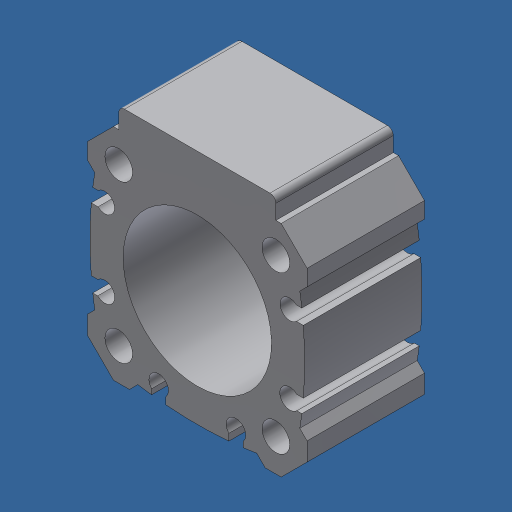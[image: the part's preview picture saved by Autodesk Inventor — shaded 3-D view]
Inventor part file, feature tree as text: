
AUTODESK INVENTOR PART (.ipt)
format: ipt  version: 2024.3 (Build 283343000, 343)  size: 252,928 bytes
history: native  units: mm (DEFAULTED — no unit token found)
features: other x1, extrude x1, sketch x1
ambient origin geometry x8: Origin, YZ Plane, XZ Plane, XY Plane, X Axis, Y Axis, Z Axis, Center Point
bodies: Body1 (feature_tree)
feature tree (3):
  other  "Finish - None"
  extrude  "PHD, 32MM"  Depth=54.69358mm
  sketch  "Sketch1"  dims[d0=54.69358mm d2=54.69358mm d3=155.869159mm d4=155.869159mm d6=32.106mm d7=27.991mm d8=2.54mm d10=15.7355mm d11=26.721mm d12=18.146886mm d13=23.52mm d14=135.0deg d15=17.916886mm d16=3.488886mm d17=135.0deg d18=22.174mm d19=9.8935mm d22=22.610478mm d23=20.015mm d24=8.357mm d25=4.242mm d26=6.8205mm d27=8.357mm d28=4.335353mm d29=6.8205mm d30=9.8935mm d31=77.93458mm d32=22.174mm d33=12.852mm d34=45.0deg d35=14.428mm d37=18.405886mm d38=135.0deg d39=24.009mm d40=77.93458mm d41=135.0deg d42=14.687mm d43=20.015mm d44=8.357mm d45=4.242mm d46=9.8935mm d47=6.8205mm d48=77.93458mm d49=77.93458mm d50=17.0mm d51=17.0mm d52=6.0mm d53=17.0mm d54=6.0mm d55=25.4mm d56=0.0mm]
